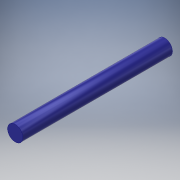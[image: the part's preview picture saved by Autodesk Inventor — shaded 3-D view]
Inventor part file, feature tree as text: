
AUTODESK INVENTOR PART (.ipt)
format: ipt  version: 2019 (Build 230136000, 136)  size: 98,304 bytes
history: native  units: mm
features: extrude x1, sketch x1
ambient origin geometry x8: Origin, YZ Plane, XZ Plane, XY Plane, X Axis, Y Axis, Z Axis, Center Point
bodies: Solid1 (feature_tree)
feature tree (2):
  extrude  "Extrusion1"  Depth=34.0mm TaperAngle=0.0deg
  sketch  "Sketch1"  dims[d0=3.5mm d1=34.0mm d2=0.0mm]
